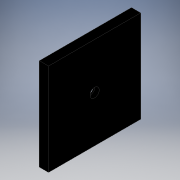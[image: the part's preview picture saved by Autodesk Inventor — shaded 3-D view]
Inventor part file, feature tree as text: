
AUTODESK INVENTOR PART (.ipt)
format: ipt  version: 2019 (Build 230136000, 136)  size: 151,552 bytes
history: native  units: mm
features: other x98, sketch x2, extrude x1, hole x1
ambient origin geometry x8: Origin, YZ Plane, XZ Plane, XY Plane, X Axis, Y Axis, Z Axis, Center Point
bodies: Solid1 (feature_tree)
feature tree (102):
  extrude  "Extrusion1"  TaperAngle=0.0deg  [1 undecoded]
  hole  "Hole1"  [1 undecoded]
  other  "CS_ANBAU_CAP_XY"
  other  "CS_ANBAU_CAP_YZ"
  other  "CS_ANBAU_CAP_ZX"
  other  "CS_ANBAU_CAP_X"
  other  "CS_ANBAU_CAP_Y"
  other  "CS_ANBAU_CAP_Z"
  other  "CS_ANBAU_CAP_Center"
  other  "CS_ANBAU_CAP_90_XY"
  other  "CS_ANBAU_CAP_90_YZ"
  other  "CS_ANBAU_CAP_90_ZX"
  other  "CS_ANBAU_CAP_90_X"
  other  "CS_ANBAU_CAP_90_Y"
  other  "CS_ANBAU_CAP_90_Z"
  other  "CS_ANBAU_CAP_90_Center"
  other  "IB_1_XY"
  other  "IB_1_YZ"
  other  "IB_1_ZX"
  other  "IB_1_X"
  other  "IB_1_Y"
  other  "IB_1_Z"
  other  "IB_1_Center"
  other  "IB_10_XY"
  other  "IB_10_YZ"
  other  "IB_10_ZX"
  other  "IB_10_X"
  other  "IB_10_Y"
  other  "IB_10_Z"
  other  "IB_10_Center"
  other  "IB_11_XY"
  other  "IB_11_YZ"
  other  "IB_11_ZX"
  other  "IB_11_X"
  other  "IB_11_Y"
  other  "IB_11_Z"
  other  "IB_11_Center"
  other  "IB_12_XY"
  other  "IB_12_YZ"
  other  "IB_12_ZX"
  other  "IB_12_X"
  other  "IB_12_Y"
  other  "IB_12_Z"
  other  "IB_12_Center"
  other  "IB_2_XY"
  other  "IB_2_YZ"
  other  "IB_2_ZX"
  other  "IB_2_X"
  other  "IB_2_Y"
  other  "IB_2_Z"
  other  "IB_2_Center"
  other  "IB_3_XY"
  other  "IB_3_YZ"
  other  "IB_3_ZX"
  other  "IB_3_X"
  other  "IB_3_Y"
  other  "IB_3_Z"
  other  "IB_3_Center"
  other  "IB_4_XY"
  other  "IB_4_YZ"
  other  "IB_4_ZX"
  other  "IB_4_X"
  other  "IB_4_Y"
  other  "IB_4_Z"
  other  "IB_4_Center"
  other  "IB_5_XY"
  other  "IB_5_YZ"
  other  "IB_5_ZX"
  other  "IB_5_X"
  other  "IB_5_Y"
  other  "IB_5_Z"
  other  "IB_5_Center"
  other  "IB_6_XY"
  other  "IB_6_YZ"
  other  "IB_6_ZX"
  other  "IB_6_X"
  other  "IB_6_Y"
  other  "IB_6_Z"
  other  "IB_6_Center"
  other  "IB_7_XY"
  other  "IB_7_YZ"
  other  "IB_7_ZX"
  other  "IB_7_X"
  other  "IB_7_Y"
  other  "IB_7_Z"
  other  "IB_7_Center"
  other  "IB_8_XY"
  other  "IB_8_YZ"
  other  "IB_8_ZX"
  other  "IB_8_X"
  other  "IB_8_Y"
  other  "IB_8_Z"
  other  "IB_8_Center"
  other  "IB_9_XY"
  other  "IB_9_YZ"
  other  "IB_9_ZX"
  other  "IB_9_X"
  other  "IB_9_Y"
  other  "IB_9_Z"
  other  "IB_9_Center"
  sketch  "Skizze_1"  dims[d0=4.0mm d1=0.0mm]
  sketch  "Sketch2"  dims[d2=4.0mm d3=6.0mm d4=8.1mm d5=2.0mm d6=90.0deg d7=4.0mm d8=0.0mm d9=0.0mm d10=0.0mm d11=0.0mm d12=0.0mm d13=0.0mm d14=0.0mm d15=0.0mm d16=0.0mm d17=0.0mm d18=0.0mm d19=0.0mm d20=0.0mm]
note: 2 required parameter values undecoded (feature->parameter linkage not recoverable at this tier; creation-order binding heuristic only, values carry confidence <= 0.55)
